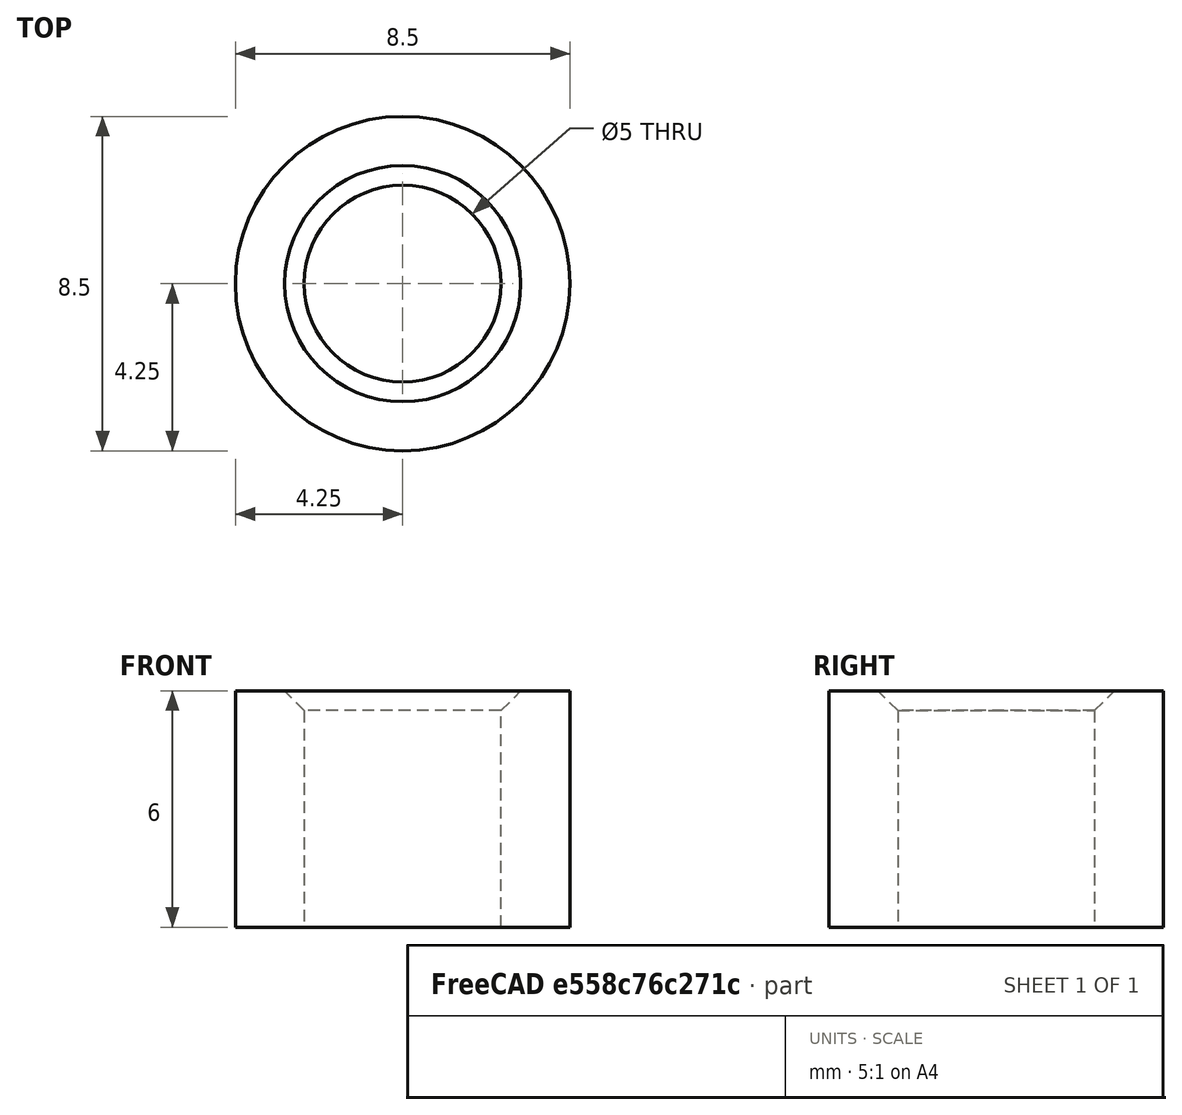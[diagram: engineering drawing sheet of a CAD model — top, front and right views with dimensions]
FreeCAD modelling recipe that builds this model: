
FCSTD DOCUMENT  (FreeCAD 0.19R24276 (Git))
Label: axis_fix_d5_d8_5__h6
License: All rights reserved
LicenseURL: http://en.wikipedia.org/wiki/All_rights_reserved
objects: Sketcher::SketchObject×1, PartDesign::Pad×1, PartDesign::Chamfer×1, PartDesign::Body×1
note: 6 computed .brp shape members not serialized (recipe doc carries the construction recipe); baked Part::Feature solids carry a one-line shape summary decoded from their .brp

FEATURE [Sketcher::SketchObject] Sketch
  FullyConstrained = true
  MapMode = 5
  Support = -> [XY_Plane]
  sketch-geometry (2):
    g0: Circle CenterX=0 CenterY=0 CenterZ=0 NormalX=0 NormalY=0 NormalZ=1 AngleXU=0 Radius=2.5
    g1: Circle CenterX=0 CenterY=0 CenterZ=0 NormalX=0 NormalY=0 NormalZ=1 AngleXU=0 Radius=4.25
  constraints (4):
    c: Coincident(g0,g-1)
    c: Diameter(g0) = 5
    c: Coincident(g1,g0)
    c: Diameter(g1) = 8.5
FEATURE [PartDesign::Pad] Pad
  Direction = (1,1,1)
  Length = 6
  Length2 = 100
  Profile = -> Sketch
  Type = 0
FEATURE [PartDesign::Chamfer] Chamfer
  Angle = 45
  Base = -> Pad [Edge6]
  BaseFeature = -> Pad
  ChamferType = 0
  FlipDirection = false
  Size = 0.5
  Size2 = 1
  SupportTransform = false
FEATURE [PartDesign::Body] Body
  Group = -> [Sketch,Pad,Chamfer]
  Origin = -> Origin
  Tip = -> Chamfer
